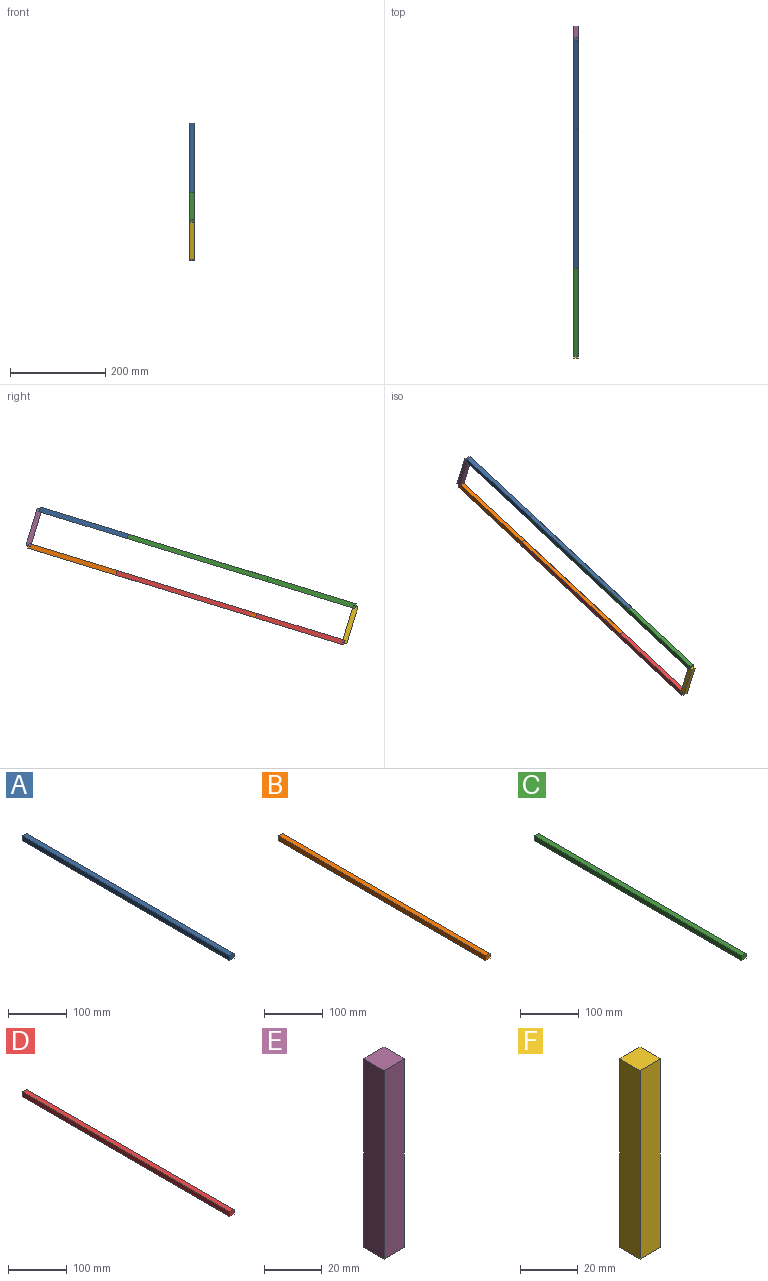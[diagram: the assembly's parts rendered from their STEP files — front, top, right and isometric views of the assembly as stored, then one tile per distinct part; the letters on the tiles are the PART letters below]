
ASSEMBLY  parts=6 mates=7
PART A: 6 faces, bbox 10x500x10 mm
  f0: plane 500x10mm, normal (0,0,-1), area 5000mm2, adj f1,f3,f4,f5
  f1: plane 10x10mm, normal (0,1,0), area 100mm2, adj f0,f2,f4,f5
  f2: plane 500x10mm, normal (0,0,1), area 5000mm2, adj f1,f3,f4,f5
  f3: plane 10x10mm, normal (0,-1,0), area 100mm2, adj f0,f2,f4,f5
  f4: plane 500x10mm, normal (1,0,0), area 5000mm2, adj f0,f1,f2,f3
  f5: plane 500x10mm, normal (-1,0,0), area 5000mm2, adj f0,f1,f2,f3
PART B: 6 faces, bbox 10x500x10 mm
  f0: plane 10x10mm, normal (0,1,0), area 100mm2, adj f1,f3,f4,f5
  f1: plane 500x10mm, normal (0,0,1), area 5000mm2, adj f0,f2,f4,f5
  f2: plane 10x10mm, normal (0,-1,0), area 100mm2, adj f1,f3,f4,f5
  f3: plane 500x10mm, normal (0,0,-1), area 5000mm2, adj f0,f2,f4,f5
  f4: plane 500x10mm, normal (1,0,0), area 5000mm2, adj f0,f1,f2,f3
  f5: plane 500x10mm, normal (-1,0,0), area 5000mm2, adj f0,f1,f2,f3
PART C: 6 faces, bbox 10x500x10 mm
  f0: plane 10x10mm, normal (0,-1,0), area 100mm2, adj f1,f3,f4,f5
  f1: plane 500x10mm, normal (0,0,-1), area 5000mm2, adj f0,f2,f4,f5
  f2: plane 10x10mm, normal (0,1,0), area 100mm2, adj f1,f3,f4,f5
  f3: plane 500x10mm, normal (0,0,1), area 5000mm2, adj f0,f2,f4,f5
  f4: plane 500x10mm, normal (1,0,0), area 5000mm2, adj f0,f1,f2,f3
  f5: plane 500x10mm, normal (-1,0,0), area 5000mm2, adj f0,f1,f2,f3
PART D: 6 faces, bbox 10x500x10 mm
  f0: plane 500x10mm, normal (0,0,1), area 5000mm2, adj f1,f3,f4,f5
  f1: plane 10x10mm, normal (0,-1,0), area 100mm2, adj f0,f2,f4,f5
  f2: plane 500x10mm, normal (0,0,-1), area 5000mm2, adj f1,f3,f4,f5
  f3: plane 10x10mm, normal (0,1,0), area 100mm2, adj f0,f2,f4,f5
  f4: plane 500x10mm, normal (1,0,0), area 5000mm2, adj f0,f1,f2,f3
  f5: plane 500x10mm, normal (-1,0,0), area 5000mm2, adj f0,f1,f2,f3
PART E: 6 faces, bbox 10x10x80 mm
  f0: plane 10x10mm, normal (0,0,1), area 100mm2, adj f1,f3,f4,f5
  f1: plane 80x10mm, normal (0,-1,0), area 800mm2, adj f0,f2,f4,f5
  f2: plane 10x10mm, normal (0,0,-1), area 100mm2, adj f1,f3,f4,f5
  f3: plane 80x10mm, normal (0,1,0), area 800mm2, adj f0,f2,f4,f5
  f4: plane 80x10mm, normal (1,0,0), area 800mm2, adj f0,f1,f2,f3
  f5: plane 80x10mm, normal (-1,0,0), area 800mm2, adj f0,f1,f2,f3
PART F: 6 faces, bbox 10x10x80 mm
  f0: plane 10x10mm, normal (0,0,1), area 100mm2, adj f1,f3,f4,f5
  f1: plane 80x10mm, normal (0,-1,0), area 800mm2, adj f0,f2,f4,f5
  f2: plane 10x10mm, normal (0,0,-1), area 100mm2, adj f1,f3,f4,f5
  f3: plane 80x10mm, normal (0,1,0), area 800mm2, adj f0,f2,f4,f5
  f4: plane 80x10mm, normal (1,0,0), area 800mm2, adj f0,f1,f2,f3
  f5: plane 80x10mm, normal (-1,0,0), area 800mm2, adj f0,f1,f2,f3
PLACE A rot(axis=(1,0,0),17deg) t=(-162.74,308.42,-14.66)mm
PLACE B rot(axis=(1,0,0),17deg) t=(-162.74,305.49,-5.1)mm
PLACE C rot(axis=(1,0,0),17deg) t=(-162.74,168.1,-81.02)mm
PLACE D rot(axis=(1,0,0),17deg) t=(-162.74,165.17,-71.46)mm
PLACE E rot(axis=(1,0,0),17deg) t=(-162.74,292.62,-14.27)mm
PLACE F rot(axis=(1,0,0),17deg) t=(-162.74,180.98,-71.85)mm
MATE cylindrical D.f3 <-> B.f2  axis (0,0.96,0.29) through (-157.74,580.19,43.49)mm
MATE revolute F.f4 <-> C.f4  axis (1,0,0) through (-152.74,78.7,-26.62)mm
MATE revolute A.f4 <-> E.f4  axis (1,0,0) through (-152.74,741.93,176.77)mm
MATE revolute E.f4 <-> B.f4  axis (1,0,0) through (-152.74,765.39,100.29)mm
MATE cylindrical C.f2 <-> A.f3  axis (0,0.96,0.29) through (-157.74,556.73,119.98)mm
MATE revolute F.f4 <-> D.f4  axis (1,0,0) through (-152.74,102.16,-103.11)mm
MATE slider F.f3 <-> E.f1  axis (0,0.96,0.29) through (-157.74,95.21,-63.4)mm
